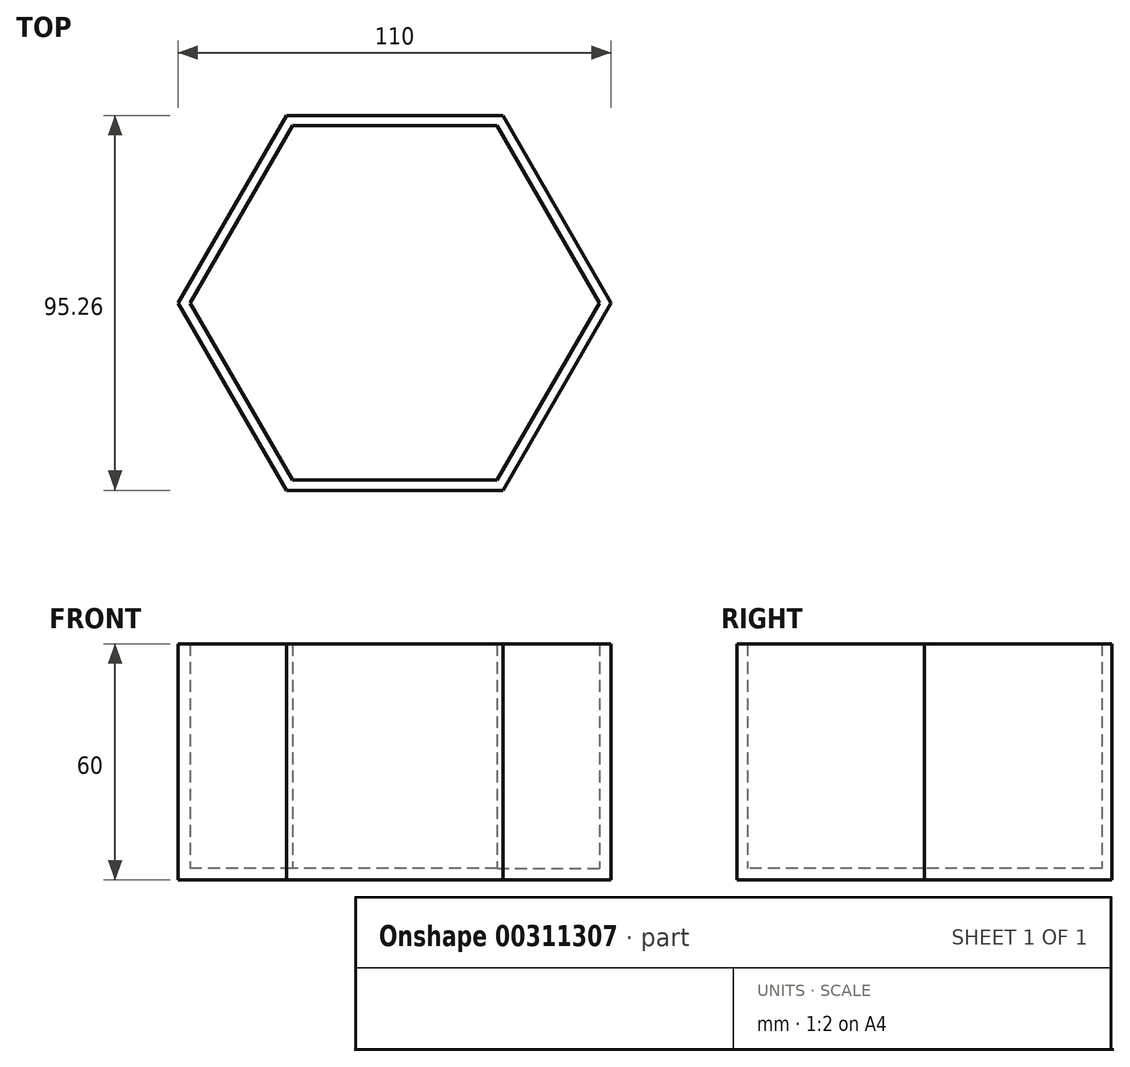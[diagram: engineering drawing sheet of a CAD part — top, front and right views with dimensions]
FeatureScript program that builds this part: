
annotation { "Feature Type Name" : "Feature", "Feature Type Description" : "" }
export const myFeature = defineFeature(function(context is Context, id is Id, definition is map)
    precondition{}
    {
        {
            var Q0;
            Q0=qCreatedBy(makeId("Top.planeOp"),FACE);
            var sketch = newSketch(context, id + "F0", { "sketchPlane" : qUnion([Q0])});
            skCircle(sketch, "E0.cCircle", {"center": v(0, 0) * mm, "radius": 55 * mm, "construction": true});
            skLineSegment(sketch, "E0.0", {"start": v(55, 0) * mm, "end": v(27.5, -47.63) * mm});
            skLineSegment(sketch, "E0.1", {"start": v(27.5, -47.63) * mm, "end": v(-27.5, -47.63) * mm});
            skLineSegment(sketch, "E0.2", {"start": v(-27.5, -47.63) * mm, "end": v(-55, 0) * mm});
            skLineSegment(sketch, "E0.3", {"start": v(-55, 0) * mm, "end": v(-27.5, 47.63) * mm});
            skLineSegment(sketch, "E0.4", {"start": v(-27.5, 47.63) * mm, "end": v(27.5, 47.63) * mm});
            skLineSegment(sketch, "E0.5", {"start": v(27.5, 47.63) * mm, "end": v(55, 0) * mm});
            skCircle(sketch, "E1.cCircle", {"center": v(0, 0) * mm, "radius": 52 * mm, "construction": true});
            skLineSegment(sketch, "E1.0", {"start": v(52, 0) * mm, "end": v(26, -45.03) * mm});
            skLineSegment(sketch, "E1.1", {"start": v(26, -45.03) * mm, "end": v(-26, -45.03) * mm});
            skLineSegment(sketch, "E1.2", {"start": v(-26, -45.03) * mm, "end": v(-52, 0) * mm});
            skLineSegment(sketch, "E1.3", {"start": v(-52, 0) * mm, "end": v(-26, 45.03) * mm});
            skLineSegment(sketch, "E1.4", {"start": v(-26, 45.03) * mm, "end": v(26, 45.03) * mm});
            skLineSegment(sketch, "E1.5", {"start": v(26, 45.03) * mm, "end": v(52, 0) * mm});
            skSolve(sketch);
        }
        {
            var Q0;
            Q0=makeQuery(id+"F0.imprint","IMPRINT",FACE,{"disambiguationData":[TD([[makeQuery(id+"F0.imprint","IMPRINT",EDGE,{"derivedFrom":sQuery(id+"F0.wireOp",EDGE,"E0.0")}),-1.0]])]});
            extrude(context, id + "F1", {"entities" : qUnion([Q0]), "depth" : 60 * mm});
        }
        {
            var Q0;
            Q0=makeQuery(id+"F0.imprint","IMPRINT",FACE,{"disambiguationData":[TD([[makeQuery(id+"F0.imprint","IMPRINT",EDGE,{"derivedFrom":sQuery(id+"F0.wireOp",EDGE,"E1.0")}),-1.0]])]});
            extrude(context, id + "F2", {"entities" : qUnion([Q0]), "operationType" : NewBodyOperationType.ADD, "depth" : 3 * mm});
        }
    });
